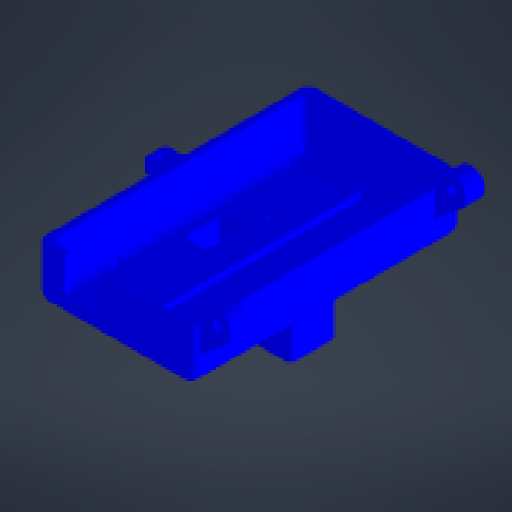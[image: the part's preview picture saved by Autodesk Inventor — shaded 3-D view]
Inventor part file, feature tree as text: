
AUTODESK INVENTOR PART (.ipt)
format: ipt  version: 2024 (Build 280153000, 153)  size: 612,864 bytes
history: native  units: mm
features: other x18, reference x12, sketch x11, extrude x11, fillet x6, mirror x2, projected_geometry x2
ambient origin geometry x8: Origin, YZ Plane, XZ Plane, XY Plane, X Axis, Y Axis, Z Axis, Center Point
bodies: Body1 (feature_tree)
feature tree (62):
  other  "Твердое тело1"
  sketch  "Эскиз1"
  other  "РабПлоскость1"
  extrude  "Выдавливание1"  Depth=15.0mm
  extrude  "Выдавливание2"  Depth=15.0mm
  extrude  "Выдавливание3"  Depth=3.0mm
  extrude  "Выдавливание4"  Depth=10.0mm TaperAngle=0.0deg
  fillet  "Сопряжение3"  Radius=3.0mm
  extrude  "Выдавливание5"  Depth=3.0mm
  extrude  "Выдавливание6"  Depth=3.0mm
  other  "Непосредственное редактирование1"
  extrude  "Выдавливание7"  Depth=17.0mm TaperAngle=0.0deg
  fillet  "Сопряжение5"  Radius=3.0mm
  fillet  "Сопряжение6"  Radius=3.0mm
  other  "РабПлоскость3"
  extrude  "Выдавливание10"  Depth=3.0mm
  other  "РабПлоскость6"
  mirror  "Зеркальное отражение1"
  fillet  "Сопряжение7"  Radius=20.0mm
  other  "РабПлоскость7"
  extrude  "Выдавливание11"  Depth=4.0mm
  fillet  "Сопряжение8"  Radius=3.0mm
  fillet  "Сопряжение9"  Radius=6.0mm
  extrude  "Выдавливание12"  Depth=50.0mm
  extrude  "Выдавливание13"  Depth=3.0mm
  other  "РабПлоскость8"
  mirror  "Зеркальное отражение2"
  reference  "Ссылка1"
  reference  "Ссылка2"
  reference  "Ссылка3"
  reference  "Ссылка4"
  sketch  "Эскиз2"
  sketch  "Эскиз3"
  sketch  "Эскиз4"
  sketch  "Эскиз9"
  sketch  "Эскиз10"
  reference  "Ссылка5"
  reference  "Ссылка6"
  reference  "Ссылка7"
  reference  "Ссылка8"
  reference  "Ссылка9"
  reference  "Ссылка10"
  sketch  "Эскиз11"
  sketch  "Эскиз15"
  sketch  "Эскиз17"
  reference  "Ссылка20"
  reference  "Ссылка21"
  projected_geometry  "Спроецированная петля1"
  projected_geometry  "Спроецированная петля2"
  sketch  "Эскиз18"
  sketch  "Эскиз19"
  parser-record x2  (decoder bookkeeping rows leaked as tree rows — omitted from the tree; the rows remain in map.json)
  other  "main_assembly.iam"
  other  "base_assembly:1"
  other  "section:4"
  other  "main axis:1"
  other  "Arduino MEGA 2560 R3:1"
  other  "Перенос1"
  other  "shock_absorber_holder_down_200:1"
  other  "front_box.iam"
  other  "front_box_cup:1"
note: 2 file-system paths scrubbed to <path> (originals preserved in map.json)
